# Revit family: HL_Сифон для писсуаров_HL431
name_source: partatom
category: Příslušenství trubek
revit_build: Autodesk Revit 2016 (Build: 20161004_0715(x64)
units: mm (PartAtom-declared; Revit-internal decimal feet)

## family parameters
Kóta kulaté spojky = Použít průměr
Nadpis OmniClass = Liquid Waste Handling Services
Ořezat dutým tvarem při načtení = Ne
Sdílené = Ne
Typ součásti = Normální
Vždy vertikální = Ano
Založené na pracovní rovině = Ne
Číslo OmniClass = 23.70.50.00

## types (2) — shared parameters
URL = http://www.hutterer-lechner.com
Výrobce = HL Hutterer & Lechner GmbH
МАТЕРИАЛ = PP
НОРМЫ = DIN1380, DIN19541
ПРОИЗВОДИТЕЛЬНОСТЬ = 0,7l/s
ПРОПУСКНАЯ СПОСОБНОСТЬ = 0.0 m³/h
материал = Plactic - White
материал 2 = Plactic - Black
zero-valued in all types: Cena

## per-type parameters (varying)
| type | EAN | Klíčová poznámka | Komentáře k typům | Model | Popis | b | n | ВЕС | НОМИНАЛЬНЫЙ ДИАМЕТР | РАЗМЕР |
| HL431_40 | 9003076000777 | HL431/40 | Сифон DN40 для писсуаров с вертикальным выпуском | HL431/40 | Сифон для писсуаров DN40 | 104 mm | 20 mm  [stored 0.0656168 ft] | 0,25 kg | 40 mm | DN40 |
| HL431_50 | 9003076000791 | HL431/50 | Сифон DN50 для писсуаров с вертикальным выпуском | HL431/50 | Сифон для писсуаров DN50 | 110 mm | 25 mm  [stored 0.082021 ft] | 0,26 kg | 50 mm | DN50 |

note: [stored X ft] marks values corroborated as IEEE doubles in the binary element streams (Revit-internal decimal feet)
